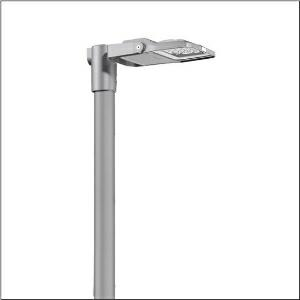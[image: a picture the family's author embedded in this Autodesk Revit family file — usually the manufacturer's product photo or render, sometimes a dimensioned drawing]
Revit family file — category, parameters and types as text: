
# Revit family: floodlight_fl_21_iq_micro___pl61_5xa7761a4c3a_000e
name_source: partatom
category: Lighting Fixtures
units: mm (PartAtom-declared; Revit-internal decimal feet)

## family parameters
Cut with Voids When Loaded = No
Host = Face
Light Source = No
Part Type = Normal
Room Calculation Point = No
Round Connector Dimension = Use Diameter
Shared = No

## types (1)
- --- (1 x LED, 3030 lm, 23.1 W, 4000K)
    Apparent Load = 23 VA
    CIE Flux Codes = 33 65 98 100 100
    Color Rendering = 70
    Color Temperature = 4000K
    Default Elevation = 1800 mm
    Description = Floodlight FL 21 iQ micro, floodlight, primary light control with lens, of PMMA, primary optical cover: protective disc, of toughened safety glass, transparent, light distribution: PL61, light emission: direct distribution, installation type: surface-mounted, LED, High Power LED, rated luminous flux: 3.030lm, luminous efficacy: 131lm/W, light colour: 740, colour temperature: 4000K, control gear: iQ Comfort/DALI, control: optimised constant luminous flux control (CLO 2.0), Desk-Remote (wireless, voltage-free reading and setting of iQ features in the workshop via application-optimized NFC function/RFID function), Light-Fading, Smart-Wire, Night-Set, Lumen-Switch, Temp-Guard, Auto-Match, with terminal, 6-pole, mains connection: 220..240V, AC, 50/60Hz, start of lifetime: 23W, end of service life: 24W, reduction: 11W, luminaire housing, of diecast aluminium, powder-coated, Siteco® metallic grey (DB 702S), corrosivity category C5 mid according to DIN EN ISO 12944, suitable for swimming pools, chlorine-resistant, sealing non-destructively replaceable, please order mast flange separately, mast bracket, of steel, galvanised, powder-coated, Siteco® metallic grey (DB 702S), protection rating (complete): IP66, insulation class (complete): insulation class II (safety insulation), certification: CE, ENEC, VDE, protection symbol: D, impact resistance: IK07, permissible operating ambient temperature: -40..+40°C, permissible operating ambient temperature for outdoor applications: -40..+50°C, standard: DIN EN 12944, LABS conformity tested according to VDMA 24364:2018-05, packaging unit: 1 piece

Light Distribution: PL61
    Height = 65 mm
    Lamp = 1 x LED
    Lamp Light Flux = 3030 lm
    Lamp Power = 23.1 W
    Lamp count = 1
    Length = 312 mm
    Luminous efficacy = 131 lm/W
    Manufacturer = Siteco
    ModVariant = No
    Model = 5XA7761A4C3A
    Number of Poles = 1
    OnlyDefault = Yes
    Power Factor = 1
    Product Name = Floodlight FL 21 iQ micro | PL61
    Product group = floodlight | pylon annexe
    ProductGroupID = 6201
    Protection Class = Protection class II
    Protection Degree = IP 66
    RLX_Detail_Level = 1
    RLX_Emergency_Light_Flux = 0 lm
    RLX_Emergency_Type = 0
    RLX_Emergency_Type_DB = No
    RlxData = <blob elided: 102045 chars, md5=633ba3ff>
    Socket = socket
    Standby Power = 0 W
    System Light Flux = 3030 lm
    System Power = 23 W
    Type Comments = factory setting: luminous flux: 100 % | dim-lin: 254 | 455 mA
    Type Image = l_1007121.jpg
    URL = http://relux.com
    VarID = @adj_215813
    Voltage = 0 V
    Weight = 0.00 kg
    Width = 230 mm

## geometry (parser evidence)
native form markers: Blend x4, Sweep x13
no freeform markers — native parametric forms only
